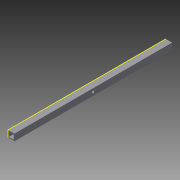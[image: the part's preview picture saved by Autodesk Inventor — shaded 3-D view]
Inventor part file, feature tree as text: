
AUTODESK INVENTOR PART (.ipt)
format: ipt  version: 2013 (Build 170138000, 138)  size: 108,544 bytes
history: native  units: in
note: dims shown in document units (in); Inventor stores cm internally (conversion verified against a paired STEP export)
features: sketch x3, extrude x2, hole x1
ambient origin geometry x8: Origin, YZ Plane, XZ Plane, XY Plane, X Axis, Y Axis, Z Axis, Center Point
bodies: Solid1 (feature_tree)
feature tree (6):
  extrude  "Extrusion1"  Depth=0.5in
  hole  "Hole1"  [1 undecoded]
  extrude  "Extrusion2"  Depth=0.168in
  sketch  "Sketch1"  dims[d0=0.5in d1=0.5in]
  sketch  "Sketch3"  dims[d3=12.0in d4=0.0in d5=0.07in]
  sketch  "Sketch4"  dims[d6=0.1875in d7=0.75in d8=0.375in d9=0.25in d10=0.5635in d11=1.0in d12=0.8108in d13=0.168in d14=0.25in d15=0.168in d16=0.25in d17=0.5in d18=0.0in]
note: 1 required parameter value undecoded (feature->parameter linkage not recoverable at this tier; creation-order binding heuristic only, values carry confidence <= 0.55)
